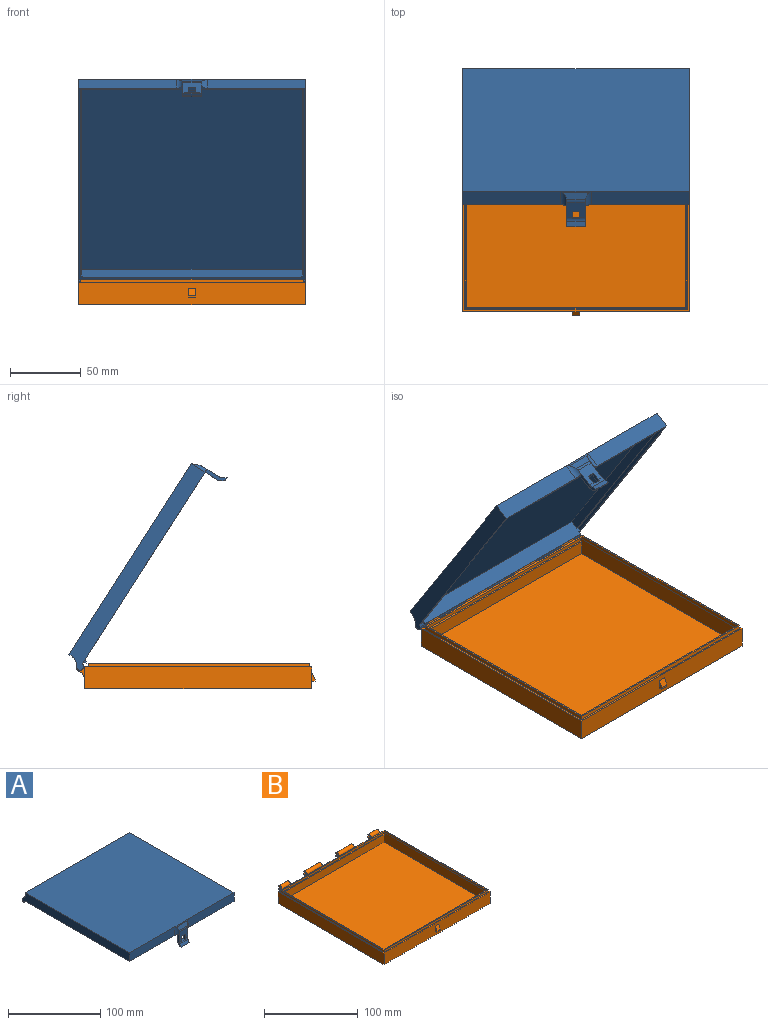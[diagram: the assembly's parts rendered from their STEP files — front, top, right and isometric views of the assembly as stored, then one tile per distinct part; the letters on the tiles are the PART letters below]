
ASSEMBLY  parts=2 mates=1
PART A: 71 faces, bbox 160x170.7x26.7 mm
  f0: plane 69.26x11.43mm, normal (0,-1,0), area 791.6mm2, adj f8,f10,f23,f70
  f1: cylinder r=1.14mm len=12.95mm, axis (1,0,0), area 93mm2, adj f29,f46
  f2: cylinder r=1.14mm len=23.11mm, axis (1,0,0), area 166mm2, adj f38,f48
  f3: cylinder r=1.14mm len=23.11mm, axis (1,0,0), area 166mm2, adj f34,f45
  f4: plane 160.02x11.43mm, normal (0,1,0), area 1062.3mm2, adj f6,f8,f10,f23,f24,f28,f29,f33
  f5: cylinder r=1.14mm len=12.95mm, axis (1,0,0), area 93mm2, adj f24,f40
  f6: plane 165.61x13.84mm, normal (-1,0,0), area 1858.8mm2, adj f4,f8,f9,f23,f30,f31,f32,f33
  f7: plane 157.48x10.92mm, normal (0,-1,0), area 1699.9mm2, adj f8,f11,f12,f14,f15,f17,f18,f19
  f8: plane 162.56x160.02mm, normal (0,0,-1), area 836.1mm2, adj f0,f4,f6,f7,f9,f10,f11,f12
  f9: plane 69.26x11.43mm, normal (0,-1,0), area 791.6mm2, adj f6,f8,f23,f69
  f10: plane 165.61x13.84mm, normal (1,0,0), area 1858.8mm2, adj f0,f4,f8,f23,f25,f26,f27,f28
  f11: plane 156.21x2.54mm, normal (-1,0,0), area 396.8mm2, adj f7,f8,f13,f18
  f12: plane 156.21x2.54mm, normal (1,0,0), area 396.8mm2, adj f7,f8,f13,f18
  f13: plane 157.48x2.54mm, normal (0,1,0), area 400mm2, adj f8,f11,f12,f18
  f14: plane 2.03x1.14mm, normal (1,0,0), area 2.3mm2, adj f7,f8,f16,f17
  f15: plane 2.03x1.14mm, normal (-1,0,0), area 2.3mm2, adj f7,f8,f16,f17
  f16: plane 154.69x2.03mm, normal (0,1,0), area 314.3mm2, adj f8,f14,f15,f17
  f17: plane 154.69x1.14mm, normal (0,0,-1), area 176.8mm2, adj f7,f14,f15,f16
  f18: plane 157.48x156.21mm, normal (0,0,-1), area 531.6mm2, adj f7,f11,f12,f13,f19,f20,f21
  f19: plane 155.07x6.35mm, normal (1,0,0), area 984.7mm2, adj f7,f18,f21,f22
  f20: plane 155.07x6.35mm, normal (-1,0,0), area 984.7mm2, adj f7,f18,f21,f22
  f21: plane 155.21x6.35mm, normal (0,1,0), area 985.6mm2, adj f18,f19,f20,f22
  f22: plane 155.21x155.07mm, normal (0,0,-1), area 24068.3mm2, adj f7,f19,f20,f21
  f23: plane 160.02x160.02mm, normal (0,0,1), area 25606.4mm2, adj f0,f4,f6,f9,f10,f68
  f24: plane 11.14x5.59mm, normal (-1,0,0), area 25.7mm2, adj f4,f5,f25,f26,f27,f28
  f25: plane 6.22x1.57mm, normal (0,-0.76,-0.65), area 12.8mm2, adj f8,f10,f24,f26
  f26: cylinder r=2.41mm len=6.22mm, axis (1,0,0), area 49.8mm2, adj f10,f24,f25,f27
  f27: plane 6.22x2.37mm, normal (0,0.63,0.77), area 19.1mm2, adj f10,f24,f26,f28
  f28: cylinder r=6.35mm len=6.22mm, axis (1,0,0), area 35mm2, adj f4,f10,f24,f27
  f29: plane 11.14x5.59mm, normal (1,0,0), area 25.7mm2, adj f1,f4,f30,f31,f32,f33
  f30: plane 6.22x1.57mm, normal (0,-0.76,-0.65), area 12.8mm2, adj f6,f8,f29,f31
  f31: cylinder r=2.41mm len=6.22mm, axis (-1,0,0), area 49.8mm2, adj f6,f29,f30,f32
  f32: plane 6.22x2.37mm, normal (0,0.63,0.77), area 19.1mm2, adj f6,f29,f31,f33
  f33: cylinder r=6.35mm len=6.22mm, axis (-1,0,0), area 35mm2, adj f4,f6,f29,f32
  f34: plane 11.14x5.59mm, normal (1,0,0), area 25.7mm2, adj f3,f4,f35,f36,f37,f39
  f35: cylinder r=2.41mm len=25.15mm, axis (-1,0,0), area 201.4mm2, adj f34,f36,f37,f38
  f36: plane 25.15x2.37mm, normal (0,0.63,0.77), area 77.1mm2, adj f34,f35,f38,f39
  f37: plane 25.15x1.57mm, normal (0,-0.76,-0.65), area 51.9mm2, adj f8,f34,f35,f38
  f38: plane 11.14x5.59mm, normal (-1,0,0), area 25.7mm2, adj f2,f4,f35,f36,f37,f39
  f39: cylinder r=6.35mm len=25.15mm, axis (-1,0,0), area 141.3mm2, adj f4,f34,f36,f38
  f40: plane 11.14x5.59mm, normal (1,0,0), area 25.7mm2, adj f4,f5,f41,f42,f43,f44
  f41: plane 25.15x1.57mm, normal (0,-0.76,-0.65), area 51.9mm2, adj f8,f40,f42,f45
  f42: cylinder r=2.41mm len=25.15mm, axis (-1,0,0), area 201.4mm2, adj f40,f41,f43,f45
  f43: plane 25.15x2.37mm, normal (0,0.63,0.77), area 77.1mm2, adj f40,f42,f44,f45
  f44: cylinder r=6.35mm len=25.15mm, axis (-1,0,0), area 141.3mm2, adj f4,f40,f43,f45
  f45: plane 11.14x5.59mm, normal (-1,0,0), area 25.7mm2, adj f3,f4,f41,f42,f43,f44
  f46: plane 11.14x5.59mm, normal (-1,0,0), area 25.7mm2, adj f1,f4,f47,f49,f50,f51
  f47: plane 25.15x1.57mm, normal (0,-0.76,-0.65), area 51.9mm2, adj f8,f46,f48,f50
  f48: plane 11.14x5.59mm, normal (1,0,0), area 25.7mm2, adj f2,f4,f47,f49,f50,f51
  f49: cylinder r=6.35mm len=25.15mm, axis (1,0,0), area 141.3mm2, adj f4,f46,f48,f51
  f50: cylinder r=2.41mm len=25.15mm, axis (1,0,0), area 201.4mm2, adj f46,f47,f48,f51
  f51: plane 25.15x2.37mm, normal (0,0.63,0.77), area 77.1mm2, adj f46,f48,f49,f50
  f52: plane 12.7x9.43mm, normal (0,1,0), area 89.1mm2, adj f8,f53,f54,f55,f56,f58,f64
  f53: plane 15.24x5.11mm, normal (1,0,0), area 38.6mm2, adj f8,f52,f59,f60,f61,f62,f64,f65
  f54: plane 15.24x5.11mm, normal (-1,0,0), area 38.6mm2, adj f8,f52,f59,f60,f61,f62,f64,f65
  f55: plane 5.33x2.54mm, normal (0,0,-1), area 13.5mm2, adj f52,f56,f58,f59
  f56: plane 6.6x2.61mm, normal (-1,0,0), area 16.8mm2, adj f52,f55,f57,f59,f64,f65
  f57: plane 5.33x2.54mm, normal (0,0,1), area 13.5mm2, adj f56,f58,f64,f65
  f58: plane 6.6x2.61mm, normal (1,0,0), area 16.8mm2, adj f52,f55,f57,f59,f64,f65
  f59: plane 13.04x12.7mm, normal (0,-1,0), area 134.9mm2, adj f53,f54,f55,f56,f58,f65,f67,f69
  f60: plane 12.7x2.63mm, normal (0,0.87,-0.5), area 38.6mm2, adj f53,f54,f64,f66
  f61: plane 12.7x1.81mm, normal (0,0,-1), area 22.9mm2, adj f53,f54,f62,f66
  f62: plane 12.7x3.27mm, normal (0,-0.87,0.5), area 47.9mm2, adj f53,f54,f61,f65
  f63: plane 17.88x4.61mm, normal (0,-0.93,0.37), area 74.6mm2, adj f67,f68,f69,f70
  f64: cylinder r=5.08mm len=12.7mm, axis (-1,0,0), area 29.2mm2, adj f52,f53,f54,f56,f57,f58,f60
  f65: cylinder r=5.08mm len=12.7mm, axis (1,0,0), area 29.2mm2, adj f53,f54,f56,f57,f58,f59,f62
  f66: cylinder r=1.27mm len=12.7mm, axis (-1,0,0), area 16.9mm2, adj f53,f54,f60,f61
  f67: cylinder r=5.08mm len=13.16mm, axis (1,0,0), area 24.8mm2, adj f59,f63,f69,f70
  f68: cylinder r=5.08mm len=21.5mm, axis (1,0,0), area 26.7mm2, adj f23,f63,f69,f70
  f69: cylinder r=5.08mm len=11.43mm, axis (0,0,1), area 46.8mm2, adj f8,f9,f59,f63,f67,f68
  f70: cylinder r=5.08mm len=11.43mm, axis (0,0,-1), area 46.8mm2, adj f0,f8,f59,f63,f67,f68
PART B: 59 faces, bbox 160x168.5x18 mm
  f0: plane 160.4x160.02mm, normal (0,0,1), area 836.8mm2, adj f1,f2,f23,f24,f25,f26,f27,f29
  f1: plane 160.02x15.24mm, normal (-1,0,0), area 2438.7mm2, adj f0,f27,f29,f30
  f2: plane 160.02x15.24mm, normal (1,0,0), area 2438.7mm2, adj f0,f27,f29,f30
  f3: cylinder r=6.35mm len=22.86mm, axis (1,0,0), area 178.7mm2, adj f7,f27,f50,f53
  f4: cylinder r=6.35mm len=12.7mm, axis (1,0,0), area 99.3mm2, adj f8,f27,f48,f51
  f5: cylinder r=6.35mm len=12.7mm, axis (1,0,0), area 99.3mm2, adj f9,f27,f46,f49
  f6: cylinder r=6.35mm len=22.86mm, axis (1,0,0), area 178.7mm2, adj f10,f27,f47,f52
  f7: cylinder r=3.17mm len=22.86mm, axis (1,0,0), area 54.1mm2, adj f3,f11,f50,f53
  f8: cylinder r=3.17mm len=12.7mm, axis (1,0,0), area 30mm2, adj f4,f12,f48,f51
  f9: cylinder r=3.17mm len=12.7mm, axis (1,0,0), area 30mm2, adj f5,f13,f46,f49
  f10: cylinder r=3.17mm len=22.86mm, axis (1,0,0), area 54.1mm2, adj f6,f14,f47,f52
  f11: plane 22.86x2.17mm, normal (0,0.17,0.98), area 50.4mm2, adj f7,f15,f50,f53
  f12: plane 12.7x2.17mm, normal (0,0.17,0.98), area 28mm2, adj f8,f16,f48,f51
  f13: plane 12.7x2.17mm, normal (0,0.17,0.98), area 28mm2, adj f9,f17,f46,f49
  f14: plane 22.86x2.17mm, normal (0,0.17,0.98), area 50.4mm2, adj f10,f18,f47,f52
  f15: cylinder r=1.27mm len=22.86mm, axis (1,0,0), area 121.6mm2, adj f11,f19,f50,f53
  f16: cylinder r=1.27mm len=12.7mm, axis (1,0,0), area 67.6mm2, adj f12,f20,f48,f51
  f17: cylinder r=1.27mm len=12.7mm, axis (1,0,0), area 67.6mm2, adj f13,f21,f46,f49
  f18: cylinder r=1.27mm len=22.86mm, axis (1,0,0), area 121.6mm2, adj f14,f22,f47,f52
  f19: plane 22.86x1.78mm, normal (0,0.17,-0.98), area 41.2mm2, adj f15,f23,f50,f53
  f20: plane 12.7x1.78mm, normal (0,0.17,-0.98), area 22.9mm2, adj f16,f24,f48,f51
  f21: plane 12.7x1.78mm, normal (0,0.17,-0.98), area 22.9mm2, adj f17,f25,f46,f49
  f22: plane 22.86x1.78mm, normal (0,0.17,-0.98), area 41.2mm2, adj f18,f26,f47,f52
  f23: cylinder r=2.79mm len=22.86mm, axis (1,0,0), area 166.8mm2, adj f0,f19,f50,f53
  f24: cylinder r=2.79mm len=12.7mm, axis (1,0,0), area 92.7mm2, adj f0,f20,f48,f51
  f25: cylinder r=2.79mm len=12.7mm, axis (1,0,0), area 92.7mm2, adj f0,f21,f46,f49
  f26: cylinder r=2.79mm len=22.86mm, axis (1,0,0), area 166.8mm2, adj f0,f22,f47,f52
  f27: plane 160.02x15.24mm, normal (0,1,0), area 1800mm2, adj f0,f1,f2,f3,f4,f5,f6,f30
  f28: plane 154.94x10.16mm, normal (0,-1,0), area 1574.2mm2, adj f32,f33,f34,f45
  f29: plane 160.02x15.24mm, normal (0,-1,0), area 2406.4mm2, adj f0,f1,f2,f30,f54,f55,f56,f58
  f30: plane 160.02x160.02mm, normal (0,0,-1), area 25606.4mm2, adj f1,f2,f27,f29
  f31: plane 154.94x12.7mm, normal (0,1,0), area 1967.7mm2, adj f32,f33,f34,f37
  f32: plane 156.21x12.7mm, normal (1,0,0), area 1971mm2, adj f0,f28,f31,f34,f38,f44,f45
  f33: plane 156.21x12.7mm, normal (-1,0,0), area 1971mm2, adj f0,f28,f31,f34,f36,f44,f45
  f34: plane 154.94x154.94mm, normal (0,0,1), area 24006.4mm2, adj f28,f31,f32,f33
  f35: plane 2.54x1.27mm, normal (0,1,0.05), area 2.9mm2, adj f0,f36,f42,f43
  f36: plane 155.07x2.54mm, normal (-1,0,0.05), area 394.1mm2, adj f33,f35,f37,f43
  f37: plane 155.21x2.54mm, normal (0,1,0.05), area 394.4mm2, adj f31,f36,f38,f43
  f38: plane 155.07x2.54mm, normal (1,0,0.05), area 394.1mm2, adj f32,f37,f39,f43
  f39: plane 2.54x1.27mm, normal (0,1,0.05), area 2.9mm2, adj f0,f38,f40,f43
  f40: plane 156.21x2.54mm, normal (-1,0,0.05), area 397mm2, adj f0,f39,f41,f43
  f41: plane 157.48x2.54mm, normal (0,-1,0.05), area 400.2mm2, adj f0,f40,f42,f43
  f42: plane 156.21x2.54mm, normal (1,0,0.05), area 397mm2, adj f0,f35,f41,f43
  f43: plane 157.21x155.94mm, normal (0,0,1), area 468.9mm2, adj f35,f36,f37,f38,f39,f40,f41,f42
  f44: plane 154.94x2.54mm, normal (0,-1,0), area 393.5mm2, adj f0,f32,f33,f45
  f45: plane 154.94x1.27mm, normal (0,0,1), area 196.8mm2, adj f28,f32,f33,f44
  f46: plane 11.77x5.98mm, normal (-1,0,0), area 26.6mm2, adj f0,f5,f9,f13,f17,f21,f25,f27
  f47: plane 11.77x5.98mm, normal (1,0,0), area 26.6mm2, adj f0,f6,f10,f14,f18,f22,f26,f27
  f48: plane 11.77x5.98mm, normal (-1,0,0), area 26.6mm2, adj f0,f4,f8,f12,f16,f20,f24,f27
  f49: plane 11.77x5.98mm, normal (1,0,0), area 26.6mm2, adj f0,f5,f9,f13,f17,f21,f25,f27
  f50: plane 11.77x5.98mm, normal (-1,0,0), area 26.6mm2, adj f0,f3,f7,f11,f15,f19,f23,f27
  f51: plane 11.77x5.98mm, normal (1,0,0), area 26.6mm2, adj f0,f4,f8,f12,f16,f20,f24,f27
  f52: plane 11.77x5.98mm, normal (-1,0,0), area 26.6mm2, adj f0,f6,f10,f14,f18,f22,f26,f27
  f53: plane 11.77x5.98mm, normal (1,0,0), area 26.6mm2, adj f0,f3,f7,f11,f15,f19,f23,f27
  f54: plane 5.08x2.54mm, normal (0,0,-1), area 12.9mm2, adj f29,f55,f56,f57
  f55: plane 6.35x2.54mm, normal (1,0,0), area 9.7mm2, adj f29,f54,f57,f58
  f56: plane 6.35x2.54mm, normal (-1,0,0), area 9.7mm2, adj f29,f54,f57,f58
  f57: plane 5.08x1.27mm, normal (0,-1,0), area 6.5mm2, adj f54,f55,f56,f58
  f58: plane 5.08x5.08mm, normal (0,-0.89,0.45), area 28.9mm2, adj f29,f55,f56,f57
PLACE A rot(axis=(-1,0,0),57.3deg) t=(-18.47,-59.56,-35.89)mm
PLACE B t=(-18.47,-85.01,-112.93)mm
MATE revolute A.f31 <-> B.f7  axis (1,0,0) through (48.84,-1.83,-97.69)mm
